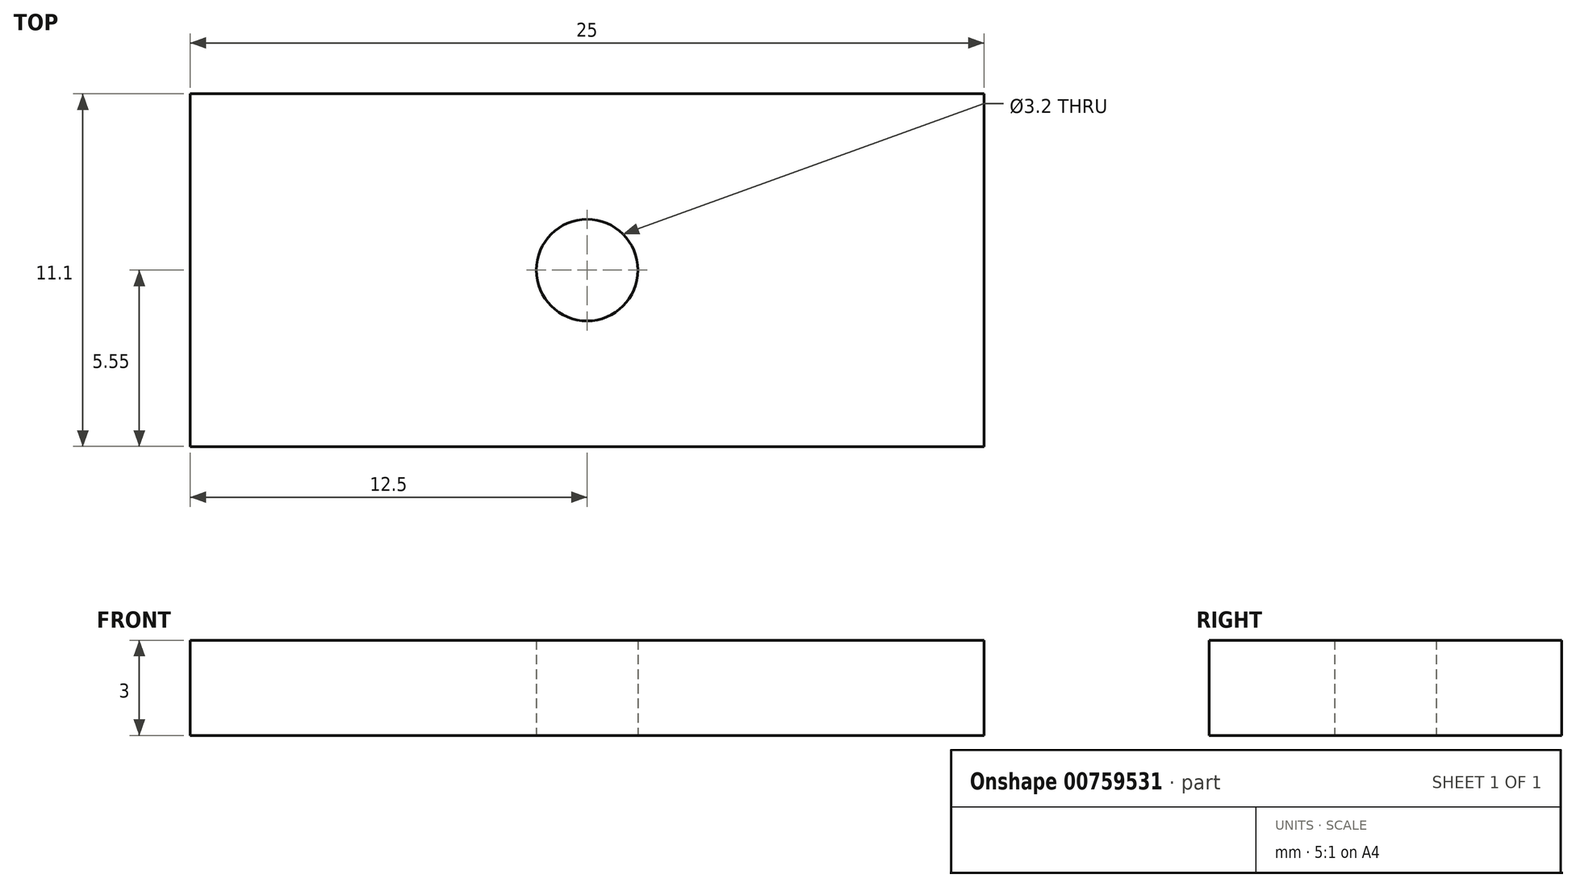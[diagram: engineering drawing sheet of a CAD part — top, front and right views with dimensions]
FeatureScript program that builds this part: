
annotation { "Feature Type Name" : "Feature", "Feature Type Description" : "" }
export const myFeature = defineFeature(function(context is Context, id is Id, definition is map)
    precondition{}
    {
        {
            var Q0;
            Q0=qCreatedBy(makeId("Top.planeOp"),FACE);
            var sketch = newSketch(context, id + "F0", { "sketchPlane" : qUnion([Q0])});
            skLineSegment(sketch, "E0.bottom", {"start": v(12.5, 5.55) * mm, "end": v(-12.5, 5.55) * mm});
            skLineSegment(sketch, "E0.top", {"start": v(12.5, -5.55) * mm, "end": v(-12.5, -5.55) * mm});
            skLineSegment(sketch, "E0.left", {"start": v(12.5, 5.55) * mm, "end": v(12.5, -5.55) * mm});
            skLineSegment(sketch, "E0.right", {"start": v(-12.5, 5.55) * mm, "end": v(-12.5, -5.55) * mm});
            skPoint(sketch, "E0.middle", {"position": v(0, 0) * mm});
            skCircle(sketch, "E1", {"center": v(0, 0) * mm, "radius": 1.6 * mm});
            skSolve(sketch);
        }
        {
            var Q0;
            Q0 = qSketchRegion(id + "F0", true);
            extrude(context, id + "F1", {"entities" : qUnion([Q0]), "depth" : 3 * mm, "offsetDistance" : 25 * mm});
        }
    });
